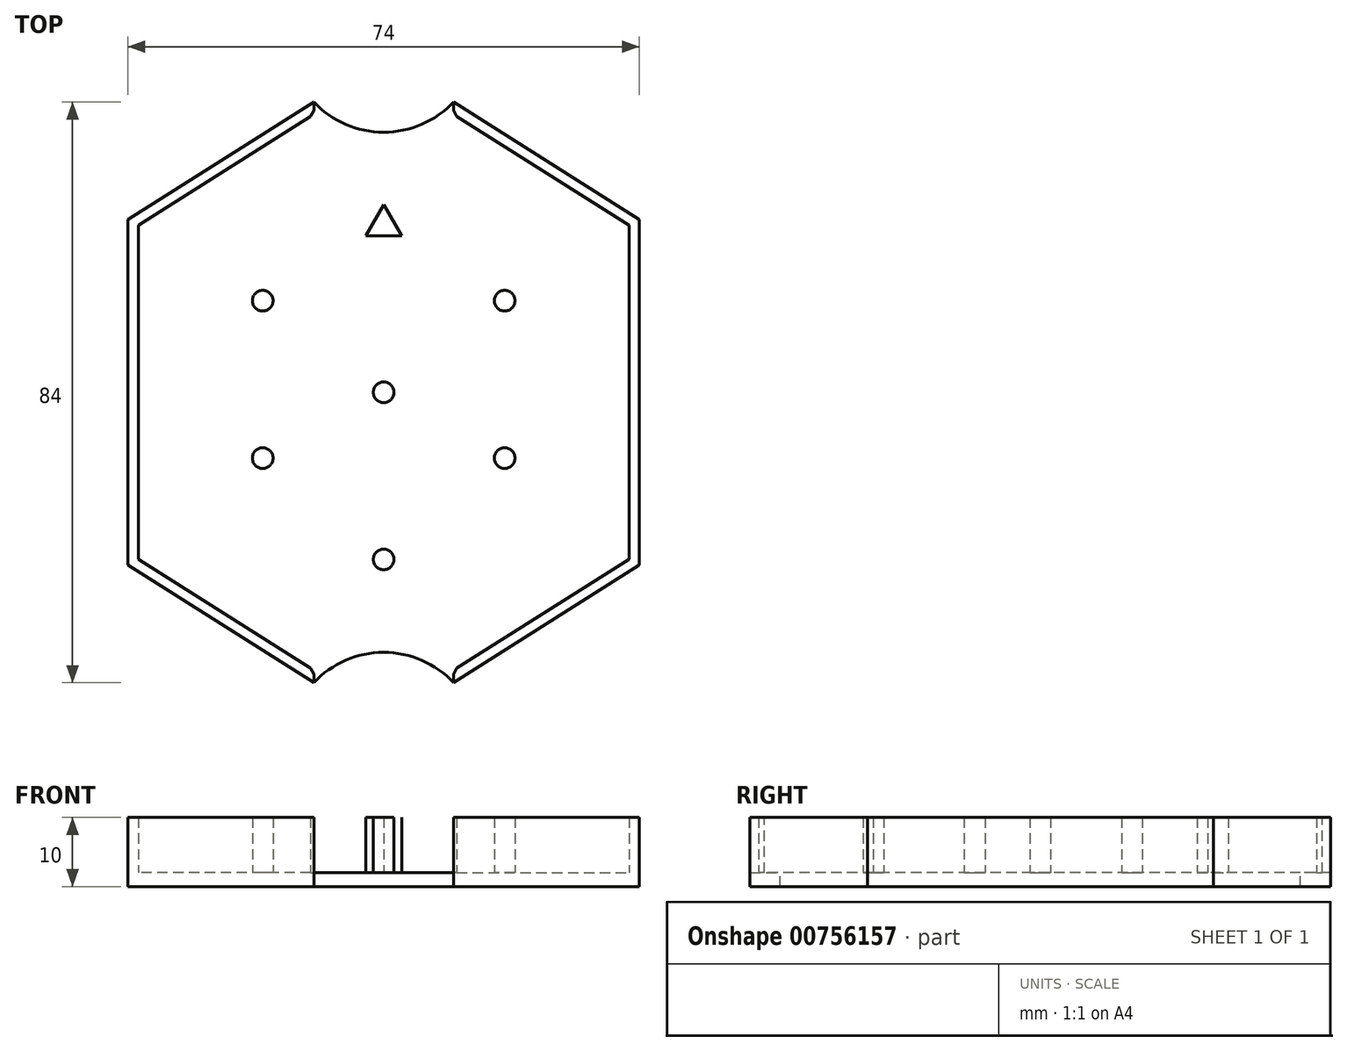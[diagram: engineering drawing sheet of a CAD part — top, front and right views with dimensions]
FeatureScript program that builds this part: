
annotation { "Feature Type Name" : "Feature", "Feature Type Description" : "" }
export const myFeature = defineFeature(function(context is Context, id is Id, definition is map)
    precondition{}
    {
        {
            var Q0;
            Q0=qCreatedBy(makeId("Top.planeOp"),FACE);
            var sketch = newSketch(context, id + "F0", { "sketchPlane" : qUnion([Q0])});
            skLineSegment(sketch, "E0.left", {"start": v(-37.82, 23.6) * mm, "end": v(-37.82, -26.4) * mm});
            skLineSegment(sketch, "E0.right", {"start": v(36.18, 23.6) * mm, "end": v(36.18, -26.4) * mm});
            skPoint(sketch, "E1", {"position": v(-37.82, 23.6) * mm});
            skPoint(sketch, "E2", {"position": v(36.18, 23.6) * mm});
            skPoint(sketch, "E3", {"position": v(36.18, -26.4) * mm});
            skPoint(sketch, "E4", {"position": v(-37.82, -26.4) * mm});
            skPoint(sketch, "E5", {"position": v(-10.92, 40.6) * mm});
            skPoint(sketch, "E6", {"position": v(-10.92, -43.4) * mm});
            skPoint(sketch, "E7", {"position": v(9.28, 40.6) * mm});
            skPoint(sketch, "E8", {"position": v(9.28, -43.4) * mm});
            skLineSegment(sketch, "E9", {"start": v(-37.82, -26.4) * mm, "end": v(-10.92, -43.4) * mm});
            skLineSegment(sketch, "E10", {"start": v(9.28, -43.4) * mm, "end": v(36.18, -26.4) * mm});
            skLineSegment(sketch, "E11", {"start": v(36.18, 23.6) * mm, "end": v(9.28, 40.6) * mm});
            skLineSegment(sketch, "E12", {"start": v(-10.92, 40.6) * mm, "end": v(-37.82, 23.6) * mm});
            skPoint(sketch, "E13.orphan", {"position": v(-37.82, 40.6) * mm});
            skPoint(sketch, "E14.orphan", {"position": v(-37.82, -32.09) * mm});
            skPoint(sketch, "E15.orphan", {"position": v(36.18, 40.6) * mm});
            skArc(sketch, "E16", {"start": v(9.28, -43.4) * mm, "mid": v(-0.82, -39.03) * mm, "end": v(-10.92, -43.4) * mm});
            skPoint(sketch, "E16.third.point", {"position": v(0, -66.7) * mm});
            skArc(sketch, "E17", {"start": v(-10.92, 40.6) * mm, "mid": v(-0.82, 36.23) * mm, "end": v(9.28, 40.6) * mm});
            skPoint(sketch, "E17.third.point", {"position": v(0, 63.9) * mm});
            skSolve(sketch);
        }
        {
            var Q0;
            Q0 = qSketchRegion(id + "F0", true);
            extrude(context, id + "F1", {"entities" : qUnion([Q0]), "oppositeDirection" : true, "depth" : 2 * mm, "offsetDistance" : 25 * mm});
        }
        {
            var Q0;
            Q0=qCreatedBy(makeId("Top.planeOp"),FACE);
            var sketch = newSketch(context, id + "F2", { "sketchPlane" : qUnion([Q0])});
            skLineSegment(sketch, "E18.right", {"start": v(36.18, 23.6) * mm, "end": v(36.18, -15.74) * mm});
            skPoint(sketch, "E19", {"position": v(-37.82, 23.6) * mm});
            skPoint(sketch, "E20", {"position": v(36.18, 23.6) * mm});
            skPoint(sketch, "E21", {"position": v(36.18, -15.74) * mm});
            skPoint(sketch, "E22", {"position": v(-37.82, -15.74) * mm});
            skPoint(sketch, "E23", {"position": v(-10.92, 40.6) * mm});
            skPoint(sketch, "E24", {"position": v(-10.92, -32.02) * mm});
            skPoint(sketch, "E25", {"position": v(9.28, 40.6) * mm});
            skPoint(sketch, "E26", {"position": v(9.28, -32.02) * mm});
            skLineSegment(sketch, "E27", {"start": v(36.18, 23.6) * mm, "end": v(9.28, 40.6) * mm});
            skLineSegment(sketch, "E28", {"start": v(-10.92, 40.6) * mm, "end": v(-37.82, 23.6) * mm});
            skPoint(sketch, "E29.orphan", {"position": v(-27.93, 39.95) * mm});
            skPoint(sketch, "E30.orphan", {"position": v(-27.93, -32.74) * mm});
            skPoint(sketch, "E31.orphan", {"position": v(36.18, 37.83) * mm});
            skLineSegment(sketch, "E32", {"start": v(-10.92, 38.83) * mm, "end": v(-36.32, 22.77) * mm});
            skLineSegment(sketch, "E33", {"start": v(34.68, -18.3) * mm, "end": v(34.68, 22.77) * mm});
            skLineSegment(sketch, "E34", {"start": v(34.68, 22.77) * mm, "end": v(9.28, 38.83) * mm});
            skLineSegment(sketch, "E35", {"start": v(-10.92, 40.6) * mm, "end": v(-10.92, 38.83) * mm});
            skLineSegment(sketch, "E36", {"start": v(9.28, 38.83) * mm, "end": v(9.28, 40.6) * mm});
            skPoint(sketch, "E37.end.orphan", {"position": v(-10.92, -31.02) * mm});
            skLineSegment(sketch, "E38", {"start": v(36.18, -15.74) * mm, "end": v(36.18, -26.4) * mm});
            skLineSegment(sketch, "E39", {"start": v(36.18, -26.4) * mm, "end": v(9.28, -43.4) * mm});
            skLineSegment(sketch, "E40", {"start": v(9.28, -43.4) * mm, "end": v(9.28, -41.62) * mm});
            skLineSegment(sketch, "E41", {"start": v(9.28, -41.62) * mm, "end": v(34.68, -25.57) * mm});
            skLineSegment(sketch, "E42", {"start": v(34.68, -25.57) * mm, "end": v(34.68, -18.3) * mm});
            skPoint(sketch, "E43.end.orphan", {"position": v(-26.93, -43.4) * mm});
            skPoint(sketch, "E44.start.orphan", {"position": v(-16.77, -26.4) * mm});
            skPoint(sketch, "E45.end.orphan", {"position": v(-37.82, -26.4) * mm});
            skLineSegment(sketch, "E46", {"start": v(-10.92, -43.4) * mm, "end": v(-10.92, -41.62) * mm});
            skLineSegment(sketch, "E47", {"start": v(-10.92, -41.62) * mm, "end": v(-31.43, -28.66) * mm});
            skLineSegment(sketch, "E48", {"start": v(-10.92, -43.4) * mm, "end": v(-37.82, -26.4) * mm});
            skLineSegment(sketch, "E49", {"start": v(-36.32, -25.57) * mm, "end": v(-31.43, -28.66) * mm});
            skPoint(sketch, "E50.end.orphan", {"position": v(-17.27, -18.3) * mm});
            skLineSegment(sketch, "E51", {"start": v(-36.32, 22.77) * mm, "end": v(-36.32, -25.57) * mm});
            skLineSegment(sketch, "E52", {"start": v(-37.82, 23.6) * mm, "end": v(-37.82, -26.4) * mm});
            skSolve(sketch);
        }
        {
            var Q0;
            Q0 = qSketchRegion(id + "F2", true);
            extrude(context, id + "F3", {"entities" : qUnion([Q0]), "operationType" : NewBodyOperationType.ADD, "depth" : 8 * mm, "offsetDistance" : 25 * mm});
        }
        {
            var Q0;
            Q0=makeQuery(id+"F1.opExtrude","CAP_FACE",FACE,{"disambiguationData":[OSD([sQuery(id+"F0.wireOp",EDGE,"E0.left"),sQuery(id+"F0.wireOp",EDGE,"E0.right"),sQuery(id+"F0.wireOp",EDGE,"E9"),sQuery(id+"F0.wireOp",EDGE,"E10"),sQuery(id+"F0.wireOp",EDGE,"E11"),sQuery(id+"F0.wireOp",EDGE,"E12"),sQuery(id+"F0.wireOp",EDGE,"E16"),sQuery(id+"F0.wireOp",EDGE,"E17")])],"isStart":true});
            var sketch = newSketch(context, id + "F4", { "sketchPlane" : qUnion([Q0])});
            skLineSegment(sketch, "E53", {"start": v(-36.32, 22.77) * mm, "end": v(34.68, 22.77) * mm, "construction": true});
            skLineSegment(sketch, "E54", {"start": v(34.68, -25.57) * mm, "end": v(-36.32, -25.57) * mm, "construction": true});
            skLineSegment(sketch, "E55", {"start": v(-0.82, 36.23) * mm, "end": v(-0.82, -39.03) * mm, "construction": true});
            skLineSegment(sketch, "E56", {"start": v(34.68, -1.4) * mm, "end": v(-36.32, -1.4) * mm, "construction": true});
            skCircle(sketch, "E57", {"center": v(-0.82, -25.57) * mm, "radius": 1.5 * mm});
            skLineSegment(sketch, "E58", {"start": v(-18.32, 36.95) * mm, "end": v(-18.32, -37.06) * mm, "construction": true});
            skLineSegment(sketch, "E59", {"start": v(16.68, 43.84) * mm, "end": v(16.68, -43.05) * mm, "construction": true});
            skCircle(sketch, "E60", {"center": v(-0.82, -1.4) * mm, "radius": 1.5 * mm});
            skCircle(sketch, "E61", {"center": v(-0.82, 22.77) * mm, "radius": 10 * mm, "construction": true});
            skCircle(sketch, "E62", {"center": v(-0.82, -1.4) * mm, "radius": 10 * mm, "construction": true});
            skCircle(sketch, "E63", {"center": v(-0.82, -25.57) * mm, "radius": 10 * mm, "construction": true});
            skCircle(sketch, "E64", {"center": v(16.68, -10.91) * mm, "radius": 1.5 * mm});
            skCircle(sketch, "E65", {"center": v(16.68, -10.91) * mm, "radius": 10 * mm, "construction": true});
            skLineSegment(sketch, "E66", {"start": v(16.68, -10.91) * mm, "end": v(16.68, 27.65) * mm, "construction": true});
            skCircle(sketch, "E67", {"center": v(16.68, 11.86) * mm, "radius": 1.5 * mm});
            skCircle(sketch, "E68", {"center": v(16.68, 11.86) * mm, "radius": 10 * mm, "construction": true});
            skLineSegment(sketch, "E69", {"start": v(16.68, 11.86) * mm, "end": v(-21.88, 11.86) * mm, "construction": true});
            skLineSegment(sketch, "E70", {"start": v(16.68, -10.91) * mm, "end": v(-23.99, -10.91) * mm, "construction": true});
            skCircle(sketch, "E71", {"center": v(-18.32, 11.86) * mm, "radius": 1.5 * mm});
            skCircle(sketch, "E72", {"center": v(-18.32, -10.91) * mm, "radius": 1.5 * mm});
            skCircle(sketch, "E73", {"center": v(-18.32, 11.86) * mm, "radius": 10 * mm, "construction": true});
            skCircle(sketch, "E74", {"center": v(-18.32, -10.91) * mm, "radius": 10 * mm, "construction": true});
            skCircle(sketch, "E75.cCircle", {"center": v(-0.82, 22.77) * mm, "radius": 1.5 * mm, "construction": true});
            skLineSegment(sketch, "E75.0", {"start": v(1.78, 21.27) * mm, "end": v(-3.42, 21.27) * mm});
            skLineSegment(sketch, "E75.1", {"start": v(-3.42, 21.27) * mm, "end": v(-0.82, 25.77) * mm});
            skLineSegment(sketch, "E75.2", {"start": v(-0.82, 25.77) * mm, "end": v(1.78, 21.27) * mm});
            skPoint(sketch, "E75.0.midPoint", {"position": v(-0.82, 21.27) * mm});
            skSolve(sketch);
        }
        {
            var Q0;
            Q0 = qSketchRegion(id + "F4", true);
            extrude(context, id + "F5", {"entities" : qUnion([Q0]), "operationType" : NewBodyOperationType.ADD, "depth" : 8 * mm, "offsetDistance" : 25 * mm});
        }
        {
            var Q0;
            Q0=makeQuery(id+"F3.opExtrude","SWEPT_EDGE",EDGE,{"disambiguationData":[OSD([sQuery(id+"F2.wireOp",EDGE,"E32"),sQuery(id+"F2.wireOp",EDGE,"E35")])]});
            var Q1;
            Q1=makeQuery(id+"F3.opExtrude","SWEPT_EDGE",EDGE,{"disambiguationData":[OSD([sQuery(id+"F2.wireOp",EDGE,"E34"),sQuery(id+"F2.wireOp",EDGE,"E36")])]});
            var Q2;
            Q2=makeQuery(id+"F3.opExtrude","SWEPT_EDGE",EDGE,{"disambiguationData":[OSD([sQuery(id+"F2.wireOp",EDGE,"E46"),sQuery(id+"F2.wireOp",EDGE,"E47")])]});
            var Q3;
            Q3=makeQuery(id+"F3.opExtrude","SWEPT_EDGE",EDGE,{"disambiguationData":[OSD([sQuery(id+"F2.wireOp",EDGE,"E40"),sQuery(id+"F2.wireOp",EDGE,"E41")])]});
            chamfer(context, id + "F6", {"entities" : qUnion([Q0, Q1, Q2, Q3]), "width" : 1 * mm, "tangentPropagation" : true});
        }
    });
